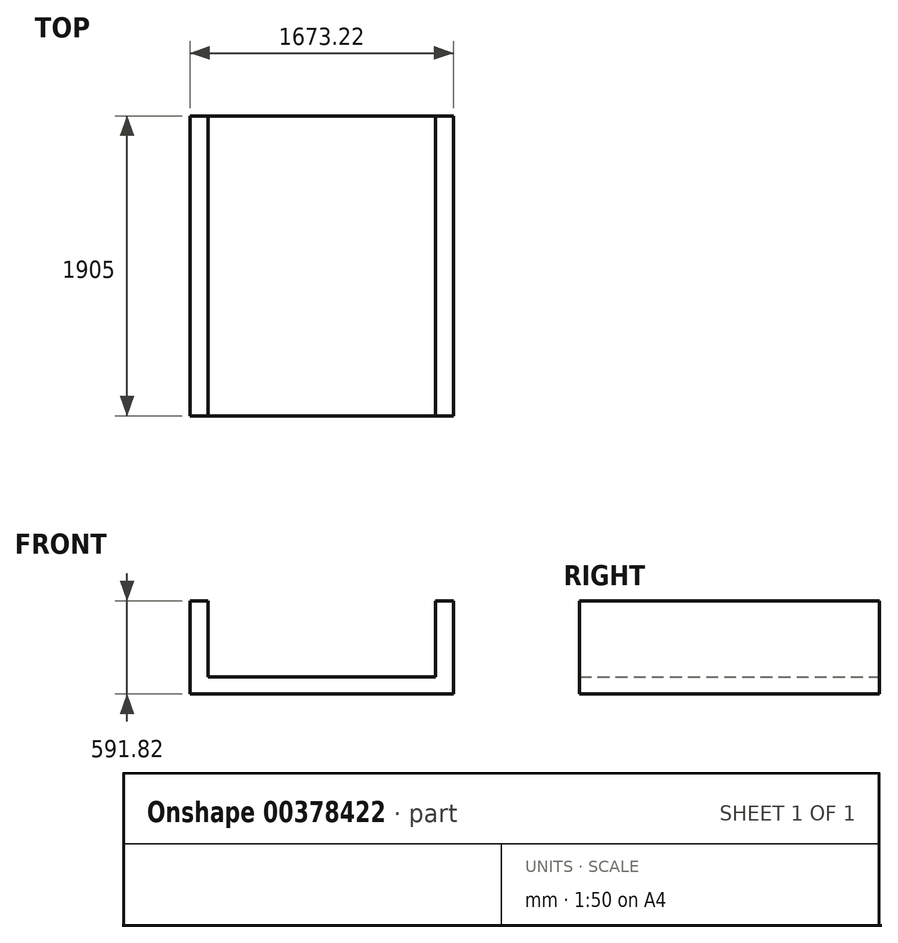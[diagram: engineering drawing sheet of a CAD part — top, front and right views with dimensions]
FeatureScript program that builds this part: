
annotation { "Feature Type Name" : "Feature", "Feature Type Description" : "" }
export const myFeature = defineFeature(function(context is Context, id is Id, definition is map)
    precondition{}
    {
        {
            var Q0;
            Q0=qCreatedBy(makeId("Front.planeOp"),FACE);
            var sketch = newSketch(context, id + "F0", { "sketchPlane" : qUnion([Q0])});
            skLineSegment(sketch, "E0", {"start": v(0, 0) * mm, "end": v(1673.22, 0) * mm});
            skLineSegment(sketch, "E1", {"start": v(1673.22, 0) * mm, "end": v(1673.22, 591.82) * mm});
            skLineSegment(sketch, "E2", {"start": v(1673.22, 591.82) * mm, "end": v(1558.92, 591.82) * mm});
            skLineSegment(sketch, "E3", {"start": v(1558.92, 591.82) * mm, "end": v(1558.92, 109.22) * mm});
            skLineSegment(sketch, "E4", {"start": v(1558.92, 109.22) * mm, "end": v(114.3, 109.22) * mm});
            skLineSegment(sketch, "E5", {"start": v(114.3, 109.22) * mm, "end": v(114.3, 591.82) * mm});
            skLineSegment(sketch, "E6", {"start": v(114.3, 591.82) * mm, "end": v(0, 591.82) * mm});
            skLineSegment(sketch, "E7", {"start": v(0, 591.82) * mm, "end": v(0, 0) * mm});
            skSolve(sketch);
        }
        {
            var Q0;
            Q0=makeQuery(id+"F0.imprint","IMPRINT",FACE,{"disambiguationData":[TD([[makeQuery(id+"F0.imprint","IMPRINT",EDGE,{"derivedFrom":sQuery(id+"F0.wireOp",EDGE,"E0")}),1.0]])]});
            extrude(context, id + "F1", {"entities" : qUnion([Q0]), "depth" : 1905 * mm});
        }
    });
